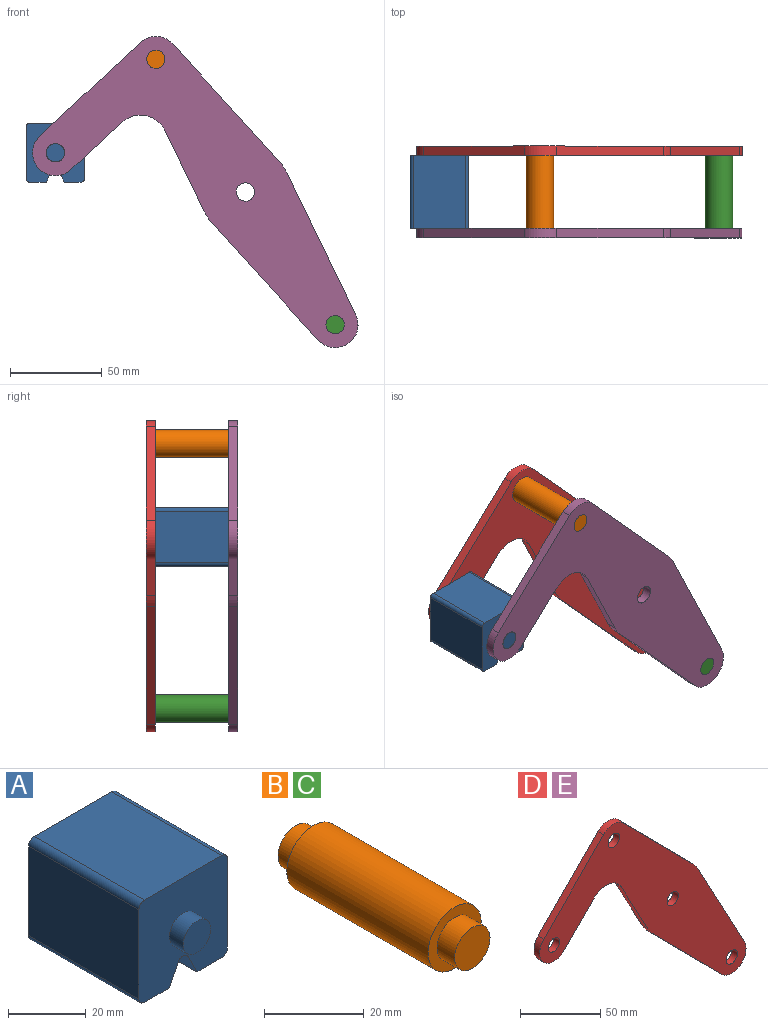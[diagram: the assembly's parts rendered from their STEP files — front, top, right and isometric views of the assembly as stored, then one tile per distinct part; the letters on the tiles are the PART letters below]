
ASSEMBLY  parts=5 mates=3
PART A: 18 faces, bbox 32.1x50x32.1 mm
  f0: plane 40x28.08mm, normal (1,0,0), area 1123.1mm2, adj f4,f10,f13,f14
  f1: plane 40x9.04mm, normal (0,0,-1), area 361.6mm2, adj f2,f4,f10,f14
  f2: plane 40x6.42mm, normal (-0.89,0,-0.45), area 287.2mm2, adj f1,f4,f10,f15
  f3: plane 40x6.42mm, normal (0.89,0,-0.45), area 287.2mm2, adj f4,f5,f10,f15
  f4: plane 32.08x32.08mm, normal (0,-1,0), area 900.6mm2, adj f0,f1,f2,f3,f5,f6,f7,f9
  f5: plane 40x9.04mm, normal (0,0,-1), area 361.6mm2, adj f3,f4,f10,f16
  f6: plane 40x28.08mm, normal (0,0,1), area 1123.1mm2, adj f4,f10,f13,f17
  f7: plane 40x28.08mm, normal (-1,0,0), area 1123.1mm2, adj f4,f10,f16,f17
  f8: plane 10x10mm, normal (0,-1,0), area 78.5mm2, adj f9
  f9: cylinder r=5mm len=10mm, axis (0,1,0), area 157.1mm2, adj f4,f8
  f10: plane 32.08x32.08mm, normal (0,1,0), area 900.6mm2, adj f0,f1,f2,f3,f5,f6,f7,f12
  f11: plane 10x10mm, normal (0,1,0), area 78.5mm2, adj f12
  f12: cylinder r=5mm len=10mm, axis (0,-1,0), area 157.1mm2, adj f10,f11
  f13: cylinder r=2mm len=40mm, axis (0,1,0), area 125.7mm2, adj f0,f4,f6,f10
  f14: cylinder r=2mm len=40mm, axis (0,-1,0), area 125.7mm2, adj f0,f1,f4,f10
  f15: cylinder r=2mm len=40mm, axis (0,1,0), area 177.1mm2, adj f2,f3,f4,f10
  f16: cylinder r=2mm len=40mm, axis (0,1,0), area 125.7mm2, adj f4,f5,f7,f10
  f17: cylinder r=2mm len=40mm, axis (0,-1,0), area 125.7mm2, adj f4,f6,f7,f10
PART B: 7 faces, bbox 15x50x15 mm
  f0: cylinder r=7.5mm len=40mm, axis (0,-1,0), area 1885mm2, adj f2,f5
  f1: cylinder r=5mm len=10mm, axis (0,1,0), area 157.1mm2, adj f2,f3
  f2: plane 15x15mm, normal (0,-1,0), area 98.2mm2, adj f0,f1
  f3: plane 10x10mm, normal (0,-1,0), area 78.5mm2, adj f1
  f4: cylinder r=5mm len=10mm, axis (0,-1,0), area 157.1mm2, adj f5,f6
  f5: plane 15x15mm, normal (0,1,0), area 98.2mm2, adj f0,f4
  f6: plane 10x10mm, normal (0,1,0), area 78.5mm2, adj f4
PART C: same geometry as B
PART D: 18 faces, bbox 181.7x5x165.8 mm
  f0: plane 43.49x23.35mm, normal (-0.88,0,-0.47), area 246.8mm2, adj f1,f14,f16,f17
  f1: cylinder r=25mm len=5.75mm, axis (0,1,0), area 35.8mm2, adj f0,f2,f16,f17
  f2: plane 61.6x60.87mm, normal (-0.71,0,-0.7), area 433mm2, adj f1,f3,f16,f17
  f3: cylinder r=12.5mm len=21.39mm, axis (0,1,0), area 178.4mm2, adj f2,f4,f16,f17
  f4: plane 76.3x40.96mm, normal (0.88,0,0.47), area 433mm2, adj f3,f5,f16,f17
  f5: cylinder r=25mm len=5.75mm, axis (0,1,0), area 35.8mm2, adj f4,f6,f16,f17
  f6: plane 61.6x60.87mm, normal (0.71,0,0.7), area 433mm2, adj f5,f7,f16,f17
  f7: cylinder r=12.5mm len=17.78mm, axis (0,1,0), area 98.9mm2, adj f6,f8,f16,f17
  f8: plane 53.35x52.71mm, normal (-0.71,0,0.7), area 375mm2, adj f7,f9,f16,f17
  f9: cylinder r=12.5mm len=21.39mm, axis (0,1,0), area 196.3mm2, adj f8,f10,f16,f17
  f10: plane 26.86x26.54mm, normal (0.71,0,-0.7), area 188.8mm2, adj f9,f14,f16,f17
  f11: cylinder r=5mm len=10mm, axis (0,1,0), area 157.1mm2, adj f16,f17
  f12: cylinder r=5mm len=10mm, axis (0,1,0), area 157.1mm2, adj f16,f17
  f13: cylinder r=5mm len=10mm, axis (0,1,0), area 157.1mm2, adj f16,f17
  f14: cylinder r=15mm len=23.89mm, axis (0,1,0), area 140.2mm2, adj f0,f10,f16,f17
  f15: cylinder r=5mm len=10mm, axis (0,1,0), area 157.1mm2, adj f16,f17
  f16: plane 181.66x165.78mm, normal (0,-1,0), area 8710.1mm2, adj f0,f1,f2,f3,f4,f5,f6,f7
  f17: plane 181.66x165.78mm, normal (0,1,0), area 8710.1mm2, adj f0,f1,f2,f3,f4,f5,f6,f7
PART E: same geometry as D
PLACE A t=(0.81,-20,4.37)mm
PLACE B rot(axis=(0,1,0),2.4deg) t=(0,-20,0)mm
PLACE C rot(axis=(0,1,0),2.4deg) t=(97.96,-20,-145.01)mm
PLACE D rot(axis=(0,1,0),2.4deg) t=(0,25,0)mm
PLACE E rot(axis=(0,1,0),2.4deg) t=(0,-20,0)mm fixed
MATE revolute E.f9 <-> A.f9  axis (0,1,0) through (-103.88,-20,21.41)mm
MATE fastened E.f3 <-> C.f0  axis (0,1,0) through (48.98,-20,-72.51)mm
MATE fastened D.f7 <-> B.f0  axis (0,-1,0) through (-48.98,20,72.51)mm
